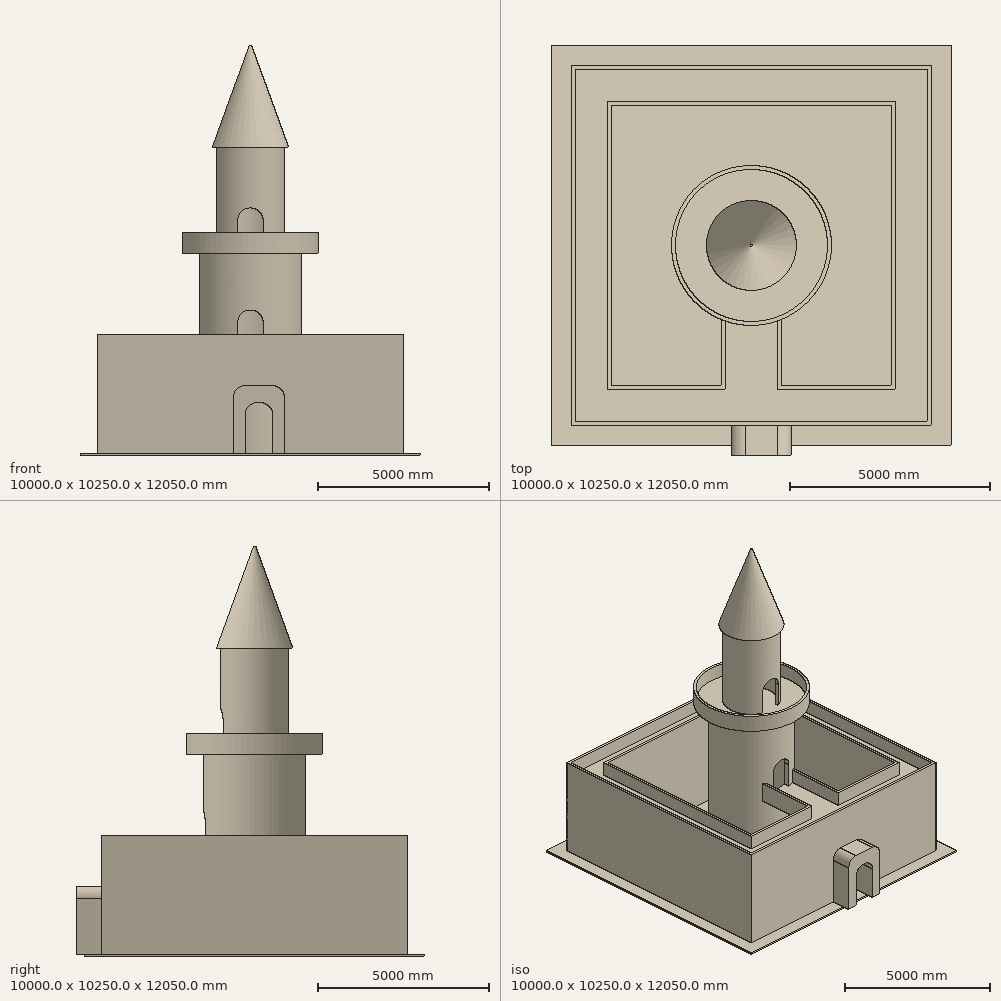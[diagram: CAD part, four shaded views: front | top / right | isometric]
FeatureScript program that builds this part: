
annotation { "Feature Type Name" : "Feature", "Feature Type Description" : "" }
export const myFeature = defineFeature(function(context is Context, id is Id, definition is map)
    precondition{}
    {
        {
            var Q0;
            Q0=qCreatedBy(makeId("Top.planeOp"),FACE);
            var sketch = newSketch(context, id + "F0", { "sketchPlane" : qUnion([Q0])});
            skLineSegment(sketch, "E0.bottom", {"start": v(5000, 5000) * mm, "end": v(-5000, 5000) * mm});
            skLineSegment(sketch, "E0.top", {"start": v(5000, -5000) * mm, "end": v(-5000, -5000) * mm});
            skLineSegment(sketch, "E0.left", {"start": v(5000, 5000) * mm, "end": v(5000, -5000) * mm});
            skLineSegment(sketch, "E0.right", {"start": v(-5000, 5000) * mm, "end": v(-5000, -5000) * mm});
            skPoint(sketch, "E0.middle", {"position": v(0, 0) * mm});
            skSolve(sketch);
        }
        {
            var Q0;
            Q0=makeQuery(id+"F0.imprint","IMPRINT",FACE,{"disambiguationData":[TD([[makeQuery(id+"F0.imprint","IMPRINT",EDGE,{"derivedFrom":sQuery(id+"F0.wireOp",EDGE,"E0.bottom")}),1.0]])]});
            extrude(context, id + "F1", {"entities" : qUnion([Q0]), "oppositeDirection" : true, "depth" : 50 * mm});
        }
        {
            var Q0;
            Q0=makeQuery(id+"F1.opExtrude","CAP_FACE",FACE,{"disambiguationData":[OSD([sQuery(id+"F0.wireOp",EDGE,"E0.bottom"),sQuery(id+"F0.wireOp",EDGE,"E0.top"),sQuery(id+"F0.wireOp",EDGE,"E0.left"),sQuery(id+"F0.wireOp",EDGE,"E0.right")])],"isStart":true});
            var sketch = newSketch(context, id + "F2", { "sketchPlane" : qUnion([Q0])});
            skCircle(sketch, "E1", {"center": v(0, 0) * mm, "radius": 1500 * mm});
            skCircle(sketch, "E2", {"center": v(0, 0) * mm, "radius": 1300 * mm});
            skSolve(sketch);
        }
        {
            var Q0;
            Q0 = qSketchRegion(id + "F2", true);
            extrude(context, id + "F3", {"entities" : qUnion([Q0]), "operationType" : NewBodyOperationType.ADD, "depth" : 3000 * mm});
        }
        {
            var Q0;
            {var subQ0=sQuery(id+"F0.wireOp",EDGE,"E0.left");var subQ1=sQuery(id+"F0.wireOp",EDGE,"E0.top");var subQ2=sQuery(id+"F0.wireOp",EDGE,"E0.right");var subQ3=sQuery(id+"F0.wireOp",EDGE,"E0.bottom");Q0=makeQuery(id+"F3.boolean.opBoolean","SPLIT",FACE,{"disambiguationData":[TD([makeQuery(id+"F1.opExtrude","SWEPT_FACE",FACE,{"disambiguationData":[OSD([subQ3])]})])],"derivedFrom":makeQuery(id+"F1.opExtrude","CAP_FACE",FACE,{"disambiguationData":[OSD([subQ3,subQ1,subQ0,subQ2])],"isStart":true})});}
            var sketch = newSketch(context, id + "F4", { "sketchPlane" : qUnion([Q0])});
            skLineSegment(sketch, "E3.bottom", {"start": v(4500, 4500) * mm, "end": v(-4500, 4500) * mm});
            skLineSegment(sketch, "E3.top", {"start": v(4500, -4500) * mm, "end": v(-4500, -4500) * mm});
            skLineSegment(sketch, "E3.left", {"start": v(4500, 4500) * mm, "end": v(4500, -4500) * mm});
            skLineSegment(sketch, "E3.right", {"start": v(-4500, 4500) * mm, "end": v(-4500, -4500) * mm});
            skPoint(sketch, "E3.middle", {"position": v(0, 0) * mm});
            skLineSegment(sketch, "E4.bottom", {"start": v(3500, 3500) * mm, "end": v(-3500, 3500) * mm});
            skLineSegment(sketch, "E4.top", {"start": v(3500, -3500) * mm, "end": v(-3500, -3500) * mm});
            skLineSegment(sketch, "E4.left", {"start": v(3500, 3500) * mm, "end": v(3500, -3500) * mm});
            skLineSegment(sketch, "E4.right", {"start": v(-3500, 3500) * mm, "end": v(-3500, -3500) * mm});
            skSolve(sketch);
        }
        {
            var Q0;
            Q0=makeQuery(id+"F4.imprint","IMPRINT",FACE,{"disambiguationData":[TD([[makeQuery(id+"F4.imprint","IMPRINT",EDGE,{"derivedFrom":sQuery(id+"F4.wireOp",EDGE,"E3.bottom")}),1.0]])]});
            extrude(context, id + "F5", {"entities" : qUnion([Q0]), "operationType" : NewBodyOperationType.ADD, "depth" : 3000 * mm});
        }
        {
            var Q0;
            Q0=makeQuery(id+"F5.opExtrude","CAP_FACE",FACE,{"disambiguationData":[OSD([sQuery(id+"F4.wireOp",EDGE,"E3.bottom"),sQuery(id+"F4.wireOp",EDGE,"E3.top"),sQuery(id+"F4.wireOp",EDGE,"E3.left"),sQuery(id+"F4.wireOp",EDGE,"E3.right"),sQuery(id+"F4.wireOp",EDGE,"E4.bottom"),sQuery(id+"F4.wireOp",EDGE,"E4.top"),sQuery(id+"F4.wireOp",EDGE,"E4.left"),sQuery(id+"F4.wireOp",EDGE,"E4.right")])],"isStart":false});
            var sketch = newSketch(context, id + "F6", { "sketchPlane" : qUnion([Q0])});
            skLineSegment(sketch, "E5", {"start": v(-750, -3500) * mm, "end": v(-750, -1299.04) * mm});
            skArc(sketch, "E6.0", {"start": v(-750, -1299.04) * mm, "mid": v(0, -1500) * mm, "end": v(750, -1299.04) * mm});
            skLineSegment(sketch, "E7.0", {"start": v(750, -3500) * mm, "end": v(-750, -3500) * mm});
            skLineSegment(sketch, "E8", {"start": v(750, -1299.04) * mm, "end": v(750, -3500) * mm});
            skLineSegment(sketch, "E9", {"start": v(0, -1500) * mm, "end": v(0, -3500) * mm, "construction": true});
            skPoint(sketch, "E10.orphan", {"position": v(-3500, -3500) * mm});
            skPoint(sketch, "E11.orphan", {"position": v(3500, -3500) * mm});
            skSolve(sketch);
        }
        {
            var Q0;
            Q0=makeQuery(id+"F6.imprint","IMPRINT",FACE,{"disambiguationData":[TD([[makeQuery(id+"F6.imprint","IMPRINT",EDGE,{"derivedFrom":sQuery(id+"F6.wireOp",EDGE,"E5")}),-1.0]])]});
            extrude(context, id + "F7", {"entities" : qUnion([Q0]), "operationType" : NewBodyOperationType.ADD, "oppositeDirection" : true, "depth" : 200 * mm});
        }
        {
            var Q0;
            Q0=makeQuery(id+"F7.boolean.opBoolean","MERGE",FACE,{"derivedFrom":[makeQuery(id+"F3.opExtrude","CAP_FACE",FACE,{"disambiguationData":[OSD([sQuery(id+"F2.wireOp",EDGE,"E1"),sQuery(id+"F2.wireOp",EDGE,"E2")])],"isStart":false}),makeQuery(id+"F5.opExtrude","CAP_FACE",FACE,{"disambiguationData":[OSD([sQuery(id+"F4.wireOp",EDGE,"E3.bottom"),sQuery(id+"F4.wireOp",EDGE,"E3.top"),sQuery(id+"F4.wireOp",EDGE,"E3.left"),sQuery(id+"F4.wireOp",EDGE,"E3.right"),sQuery(id+"F4.wireOp",EDGE,"E4.bottom"),sQuery(id+"F4.wireOp",EDGE,"E4.top"),sQuery(id+"F4.wireOp",EDGE,"E4.left"),sQuery(id+"F4.wireOp",EDGE,"E4.right")])],"isStart":false}),makeQuery(id+"F7.opExtrude","CAP_FACE",FACE,{"disambiguationData":[OSD([sQuery(id+"F6.wireOp",EDGE,"E5"),sQuery(id+"F6.wireOp",EDGE,"E6.0"),sQuery(id+"F6.wireOp",EDGE,"E7.0"),sQuery(id+"F6.wireOp",EDGE,"E8")])],"isStart":true})]});
            var sketch = newSketch(context, id + "F8", { "sketchPlane" : qUnion([Q0])});
            skCircle(sketch, "E12", {"center": v(0, 0) * mm, "radius": 1300 * mm});
            skCircle(sketch, "E13", {"center": v(0, 0) * mm, "radius": 1500 * mm});
            skSolve(sketch);
        }
        {
            var Q0;
            Q0 = qSketchRegion(id + "F8", true);
            extrude(context, id + "F9", {"entities" : qUnion([Q0]), "operationType" : NewBodyOperationType.ADD, "depth" : 3000 * mm});
        }
        {
            var Q0;
            Q0=qCreatedBy(makeId("Front.planeOp"),FACE);
            var sketch = newSketch(context, id + "F10", { "sketchPlane" : qUnion([Q0])});
            skLineSegment(sketch, "E14", {"start": v(0, 3000) * mm, "end": v(0, 3850) * mm, "construction": true});
            skArc(sketch, "E15", {"start": v(375, 3850) * mm, "mid": v(0, 4225) * mm, "end": v(-375, 3850) * mm});
            skLineSegment(sketch, "E16", {"start": v(-375, 3850) * mm, "end": v(-375, 3000) * mm});
            skLineSegment(sketch, "E17", {"start": v(-375, 3000) * mm, "end": v(375, 3000) * mm});
            skLineSegment(sketch, "E18", {"start": v(375, 3000) * mm, "end": v(375, 3850) * mm});
            skSolve(sketch);
        }
        {
            var Q0;
            Q0 = qSketchRegion(id + "F10", true);
            extrude(context, id + "F11", {"entities" : qUnion([Q0]), "operationType" : NewBodyOperationType.REMOVE, "depth" : 2000 * mm});
        }
        {
            var Q0;
            Q0=makeQuery(id+"F11.boolean.opBoolean","MERGE",FACE,{"derivedFrom":[makeQuery(id+"F7.boolean.opBoolean","MERGE",FACE,{"derivedFrom":[makeQuery(id+"F3.opExtrude","CAP_FACE",FACE,{"disambiguationData":[OSD([sQuery(id+"F2.wireOp",EDGE,"E1"),sQuery(id+"F2.wireOp",EDGE,"E2")])],"isStart":false}),makeQuery(id+"F5.opExtrude","CAP_FACE",FACE,{"disambiguationData":[OSD([sQuery(id+"F4.wireOp",EDGE,"E3.bottom"),sQuery(id+"F4.wireOp",EDGE,"E3.top"),sQuery(id+"F4.wireOp",EDGE,"E3.left"),sQuery(id+"F4.wireOp",EDGE,"E3.right"),sQuery(id+"F4.wireOp",EDGE,"E4.bottom"),sQuery(id+"F4.wireOp",EDGE,"E4.top"),sQuery(id+"F4.wireOp",EDGE,"E4.left"),sQuery(id+"F4.wireOp",EDGE,"E4.right")])],"isStart":false}),makeQuery(id+"F7.opExtrude","CAP_FACE",FACE,{"disambiguationData":[OSD([sQuery(id+"F6.wireOp",EDGE,"E5"),sQuery(id+"F6.wireOp",EDGE,"E6.0"),sQuery(id+"F6.wireOp",EDGE,"E7.0"),sQuery(id+"F6.wireOp",EDGE,"E8")])],"isStart":true})]}),makeQuery(id+"F11.opExtrude","SWEPT_FACE",FACE,{"disambiguationData":[OSD([sQuery(id+"F10.wireOp",EDGE,"E17")])]})]});
            var sketch = newSketch(context, id + "F12", { "sketchPlane" : qUnion([Q0])});
            skPoint(sketch, "E19.0", {"position": v(-3500, -3500) * mm});
            skLineSegment(sketch, "E20.0.0", {"start": v(-4500, -4500) * mm, "end": v(4500, -4500) * mm});
            skLineSegment(sketch, "E20.0.1", {"start": v(4500, -4500) * mm, "end": v(4500, 4500) * mm});
            skLineSegment(sketch, "E20.0.2", {"start": v(4500, 4500) * mm, "end": v(-4500, 4500) * mm});
            skLineSegment(sketch, "E20.0.3", {"start": v(-4500, 4500) * mm, "end": v(-4500, -4500) * mm});
            skLineSegment(sketch, "E21.0", {"start": v(-750, -3500) * mm, "end": v(-3500, -3500) * mm});
            skLineSegment(sketch, "E22.0", {"start": v(-3500, 3500) * mm, "end": v(-3500, -3500) * mm});
            skLineSegment(sketch, "E23.0", {"start": v(3500, 3500) * mm, "end": v(-3500, 3500) * mm});
            skLineSegment(sketch, "E24.0", {"start": v(3500, 3500) * mm, "end": v(3500, -3500) * mm});
            skLineSegment(sketch, "E25.0", {"start": v(3500, -3500) * mm, "end": v(750, -3500) * mm});
            skLineSegment(sketch, "E26.0", {"start": v(750, -1299.04) * mm, "end": v(750, -3500) * mm});
            skPoint(sketch, "E27.0", {"position": v(-375, -1244.74) * mm});
            skArc(sketch, "E28.0", {"start": v(-750, -1299.04) * mm, "mid": v(-700.5, -1326.39) * mm, "end": v(-650, -1351.85) * mm});
            skArc(sketch, "E29.0", {"start": v(650, -1351.85) * mm, "mid": v(700.5, -1326.39) * mm, "end": v(750, -1299.04) * mm});
            skLineSegment(sketch, "E30.0", {"start": v(-4400, -4400) * mm, "end": v(4400, -4400) * mm});
            skLineSegment(sketch, "E30.1", {"start": v(-4400, 4400) * mm, "end": v(-4400, -4400) * mm});
            skLineSegment(sketch, "E30.2", {"start": v(4400, 4400) * mm, "end": v(-4400, 4400) * mm});
            skLineSegment(sketch, "E30.3", {"start": v(4400, -4400) * mm, "end": v(4400, 4400) * mm});
            skLineSegment(sketch, "E31", {"start": v(-750, -3500) * mm, "end": v(-750, -1299.04) * mm});
            skLineSegment(sketch, "E32.0", {"start": v(-650, -3600) * mm, "end": v(-650, -1351.85) * mm});
            skLineSegment(sketch, "E32.1", {"start": v(-650, -3600) * mm, "end": v(-3600, -3600) * mm});
            skLineSegment(sketch, "E32.2", {"start": v(-3600, 3600) * mm, "end": v(-3600, -3600) * mm});
            skLineSegment(sketch, "E32.3", {"start": v(650, -1351.85) * mm, "end": v(650, -3600) * mm});
            skLineSegment(sketch, "E32.4", {"start": v(3600, -3600) * mm, "end": v(650, -3600) * mm});
            skLineSegment(sketch, "E32.5", {"start": v(3600, 3600) * mm, "end": v(3600, -3600) * mm});
            skLineSegment(sketch, "E32.6", {"start": v(3600, 3600) * mm, "end": v(-3600, 3600) * mm});
            skPoint(sketch, "E33.orphan", {"position": v(-375, -1452.37) * mm});
            skPoint(sketch, "E34.orphan", {"position": v(375, -1452.37) * mm});
            skSolve(sketch);
        }
        {
            var Q0;
            Q0=makeQuery(id+"F12.imprint","IMPRINT",FACE,{"disambiguationData":[TD([[makeQuery(id+"F12.imprint","IMPRINT",EDGE,{"derivedFrom":sQuery(id+"F12.wireOp",EDGE,"E21.0")}),1.0]])]});
            var Q1;
            Q1=makeQuery(id+"F12.imprint","IMPRINT",FACE,{"disambiguationData":[TD([[makeQuery(id+"F12.imprint","IMPRINT",EDGE,{"derivedFrom":sQuery(id+"F12.wireOp",EDGE,"E20.0.0")}),-1.0]])]});
            extrude(context, id + "F13", {"entities" : qUnion([Q0, Q1]), "operationType" : NewBodyOperationType.ADD, "depth" : 500 * mm});
        }
        {
            var Q0;
            Q0=makeQuery(id+"F9.opExtrude","CAP_FACE",FACE,{"disambiguationData":[OSD([sQuery(id+"F8.wireOp",EDGE,"E12"),sQuery(id+"F8.wireOp",EDGE,"E13")])],"isStart":false});
            var sketch = newSketch(context, id + "F14", { "sketchPlane" : qUnion([Q0])});
            skCircle(sketch, "E35", {"center": v(0, 0) * mm, "radius": 2000 * mm});
            skSolve(sketch);
        }
        {
            var Q0;
            Q0 = qSketchRegion(id + "F14", true);
            extrude(context, id + "F15", {"entities" : qUnion([Q0]), "operationType" : NewBodyOperationType.ADD, "oppositeDirection" : true, "depth" : 100 * mm});
        }
        {
            var Q0;
            Q0=makeQuery(id+"F15.boolean.opBoolean","MERGE",FACE,{"derivedFrom":[makeQuery(id+"F9.opExtrude","CAP_FACE",FACE,{"disambiguationData":[OSD([sQuery(id+"F8.wireOp",EDGE,"E12"),sQuery(id+"F8.wireOp",EDGE,"E13")])],"isStart":false}),makeQuery(id+"F15.opExtrude","CAP_FACE",FACE,{"disambiguationData":[OSD([sQuery(id+"F14.wireOp",EDGE,"E35")])],"isStart":true})]});
            var sketch = newSketch(context, id + "F16", { "sketchPlane" : qUnion([Q0])});
            skCircle(sketch, "E36.0", {"center": v(0, 0) * mm, "radius": 2000 * mm});
            skCircle(sketch, "E37.0", {"center": v(0, 0) * mm, "radius": 1900 * mm});
            skSolve(sketch);
        }
        {
            var Q0;
            Q0 = qSketchRegion(id + "F16", true);
            extrude(context, id + "F17", {"entities" : qUnion([Q0]), "operationType" : NewBodyOperationType.ADD, "depth" : 500 * mm});
        }
        {
            var Q0;
            Q0=makeQuery(id+"F15.boolean.opBoolean","MERGE",FACE,{"derivedFrom":[makeQuery(id+"F9.opExtrude","CAP_FACE",FACE,{"disambiguationData":[OSD([sQuery(id+"F8.wireOp",EDGE,"E12"),sQuery(id+"F8.wireOp",EDGE,"E13")])],"isStart":false}),makeQuery(id+"F15.opExtrude","CAP_FACE",FACE,{"disambiguationData":[OSD([sQuery(id+"F14.wireOp",EDGE,"E35")])],"isStart":true})]});
            var sketch = newSketch(context, id + "F18", { "sketchPlane" : qUnion([Q0])});
            skCircle(sketch, "E38", {"center": v(0, 0) * mm, "radius": 1000 * mm});
            skCircle(sketch, "E39.0", {"center": v(0, 0) * mm, "radius": 900 * mm});
            skSolve(sketch);
        }
        {
            var Q0;
            Q0=makeQuery(id+"F18.imprint","IMPRINT",FACE,{"disambiguationData":[TD([[makeQuery(id+"F18.imprint","IMPRINT",EDGE,{"derivedFrom":sQuery(id+"F18.wireOp",EDGE,"E38")}),1.0]])]});
            extrude(context, id + "F19", {"entities" : qUnion([Q0]), "operationType" : NewBodyOperationType.ADD, "depth" : 3000 * mm});
        }
        {
            var Q0;
            Q0=qCreatedBy(makeId("Front.planeOp"),FACE);
            var sketch = newSketch(context, id + "F20", { "sketchPlane" : qUnion([Q0])});
            skLineSegment(sketch, "E40", {"start": v(0, 6000) * mm, "end": v(0, 6850) * mm, "construction": true});
            skArc(sketch, "E41", {"start": v(375, 6850) * mm, "mid": v(0, 7225) * mm, "end": v(-375, 6850) * mm});
            skLineSegment(sketch, "E42", {"start": v(-375, 6850) * mm, "end": v(-375, 6000) * mm});
            skLineSegment(sketch, "E43", {"start": v(-375, 6000) * mm, "end": v(375, 6000) * mm});
            skLineSegment(sketch, "E44", {"start": v(375, 6000) * mm, "end": v(375, 6850) * mm});
            skSolve(sketch);
        }
        {
            var Q0;
            Q0 = qSketchRegion(id + "F20", true);
            var Q1;
            Q1=makeQuery(id+"F19.opExtrude","SWEPT_FACE",FACE,{"disambiguationData":[OSD([sQuery(id+"F18.wireOp",EDGE,"E38")])]});
            extrude(context, id + "F21", {"entities" : qUnion([Q0]), "operationType" : NewBodyOperationType.REMOVE, "endBound" : BoundingType.UP_TO_SURFACE, "endBoundEntityFace" : qUnion([Q1]), "depth" : 1500 * mm});
        }
        {
            var Q0;
            Q0=makeQuery(id+"F19.opExtrude","CAP_FACE",FACE,{"disambiguationData":[OSD([sQuery(id+"F18.wireOp",EDGE,"E38"),sQuery(id+"F18.wireOp",EDGE,"E39.0")])],"isStart":false});
            var sketch = newSketch(context, id + "F22", { "sketchPlane" : qUnion([Q0])});
            skCircle(sketch, "E45", {"center": v(0, 0) * mm, "radius": 1125 * mm});
            skSolve(sketch);
        }
        {
            var Q0;
            Q0=makeQuery(id+"F22.imprint","IMPRINT",FACE,{"disambiguationData":[TD([[makeQuery(id+"F22.imprint","IMPRINT",EDGE,{"derivedFrom":sQuery(id+"F22.wireOp",EDGE,"E45")}),1.0]])]});
            var Q1;
            Q1=makeQuery(id+"F22.imprint","IMPRINT",FACE,{"disambiguationData":[TD([[makeQuery(id+"F22.imprint","IMPRINT",EDGE,{"derivedFrom":makeQuery(id+"F19.opExtrude","CAP_EDGE",EDGE,{"disambiguationData":[OSD([sQuery(id+"F18.wireOp",EDGE,"E38")])],"isStart":false})}),1.0]])]});
            var Q2;
            Q2=makeQuery(id+"F22.imprint","IMPRINT",FACE,{"disambiguationData":[TD([[makeQuery(id+"F22.imprint","IMPRINT",EDGE,{"derivedFrom":makeQuery(id+"F19.opExtrude","CAP_EDGE",EDGE,{"disambiguationData":[OSD([sQuery(id+"F18.wireOp",EDGE,"E39.0")])],"isStart":false})}),1.0]])]});
            extrude(context, id + "F23", {"entities" : qUnion([Q0, Q1, Q2]), "operationType" : NewBodyOperationType.ADD, "depth" : 3000 * mm, "hasDraft" : true, "draftAngle" : 20 * degree, "draftPullDirection" : true});
        }
        {
            var Q0;
            Q0=makeQuery(id+"F13.boolean.opBoolean","MERGE",FACE,{"derivedFrom":[makeQuery(id+"F5.opExtrude","SWEPT_FACE",FACE,{"disambiguationData":[OSD([sQuery(id+"F4.wireOp",EDGE,"E3.top")])]}),makeQuery(id+"F13.opExtrude","SWEPT_FACE",FACE,{"disambiguationData":[OSD([sQuery(id+"F12.wireOp",EDGE,"E20.0.0")])]})]});
            var sketch = newSketch(context, id + "F24", { "sketchPlane" : qUnion([Q0])});
            skLineSegment(sketch, "E46.bottom", {"start": v(1000, 2000) * mm, "end": v(-500, 2000) * mm});
            skLineSegment(sketch, "E46.top", {"start": v(1000, 0) * mm, "end": v(-500, 0) * mm});
            skLineSegment(sketch, "E46.left", {"start": v(1000, 2000) * mm, "end": v(1000, 0) * mm});
            skLineSegment(sketch, "E46.right", {"start": v(-500, 2000) * mm, "end": v(-500, 0) * mm});
            skSolve(sketch);
        }
        {
            var Q0;
            Q0=makeQuery(id+"F24.imprint","IMPRINT",FACE,{"disambiguationData":[TD([[makeQuery(id+"F24.imprint","IMPRINT",EDGE,{"derivedFrom":sQuery(id+"F24.wireOp",EDGE,"E46.bottom")}),1.0]])]});
            extrude(context, id + "F25", {"entities" : qUnion([Q0]), "operationType" : NewBodyOperationType.ADD, "depth" : 750 * mm, "offsetDistance" : 25 * mm});
        }
        {
            var Q0;
            Q0=makeQuery(id+"F25.opExtrude","CAP_FACE",FACE,{"disambiguationData":[OSD([sQuery(id+"F24.wireOp",EDGE,"E46.bottom"),sQuery(id+"F24.wireOp",EDGE,"E46.top"),sQuery(id+"F24.wireOp",EDGE,"E46.left"),sQuery(id+"F24.wireOp",EDGE,"E46.right")])],"isStart":false});
            var sketch = newSketch(context, id + "F26", { "sketchPlane" : qUnion([Q0])});
            skLineSegment(sketch, "E47.bottom", {"start": v(-150, 0) * mm, "end": v(650, 0) * mm});
            skLineSegment(sketch, "E47.top", {"start": v(-150, 1500) * mm, "end": v(650, 1500) * mm});
            skLineSegment(sketch, "E47.left", {"start": v(-150, 0) * mm, "end": v(-150, 1500) * mm});
            skLineSegment(sketch, "E47.right", {"start": v(650, 0) * mm, "end": v(650, 1500) * mm});
            skSolve(sketch);
        }
        {
            var Q0;
            Q0=makeQuery(id+"F26.imprint","IMPRINT",FACE,{"disambiguationData":[TD([[makeQuery(id+"F26.imprint","IMPRINT",EDGE,{"derivedFrom":sQuery(id+"F26.wireOp",EDGE,"E47.bottom")}),-1.0]])]});
            extrude(context, id + "F27", {"entities" : qUnion([Q0]), "operationType" : NewBodyOperationType.REMOVE, "endBound" : BoundingType.UP_TO_NEXT, "oppositeDirection" : true, "depth" : 25 * mm, "offsetDistance" : 25 * mm});
        }
        {
            var Q0;
            Q0=makeQuery(id+"F25.opExtrude","SWEPT_EDGE",EDGE,{"disambiguationData":[OSD([sQuery(id+"F24.wireOp",EDGE,"E46.bottom"),sQuery(id+"F24.wireOp",EDGE,"E46.left")])]});
            var Q1;
            Q1=makeQuery(id+"F25.opExtrude","SWEPT_EDGE",EDGE,{"disambiguationData":[OSD([sQuery(id+"F24.wireOp",EDGE,"E46.bottom"),sQuery(id+"F24.wireOp",EDGE,"E46.right")])]});
            var Q2;
            Q2=makeQuery(id+"F27.boolean.opBoolean","COPY",EDGE,{"derivedFrom":makeQuery(id+"F27.opExtrude","SWEPT_EDGE",EDGE,{"disambiguationData":[OSD([sQuery(id+"F26.wireOp",EDGE,"E47.top"),sQuery(id+"F26.wireOp",EDGE,"E47.left")])]})});
            var Q3;
            Q3=makeQuery(id+"F27.boolean.opBoolean","COPY",EDGE,{"derivedFrom":makeQuery(id+"F27.opExtrude","SWEPT_EDGE",EDGE,{"disambiguationData":[OSD([sQuery(id+"F26.wireOp",EDGE,"E47.top"),sQuery(id+"F26.wireOp",EDGE,"E47.right")])]})});
            fillet(context, id + "F28", {"entities" : qUnion([Q0, Q1, Q2, Q3]), "tangentPropagation" : true, "radius" : 350 * mm, "defaultsChanged" : true, "vertexSettings" : [], "allowEdgeOverflow" : false});
        }
    });
